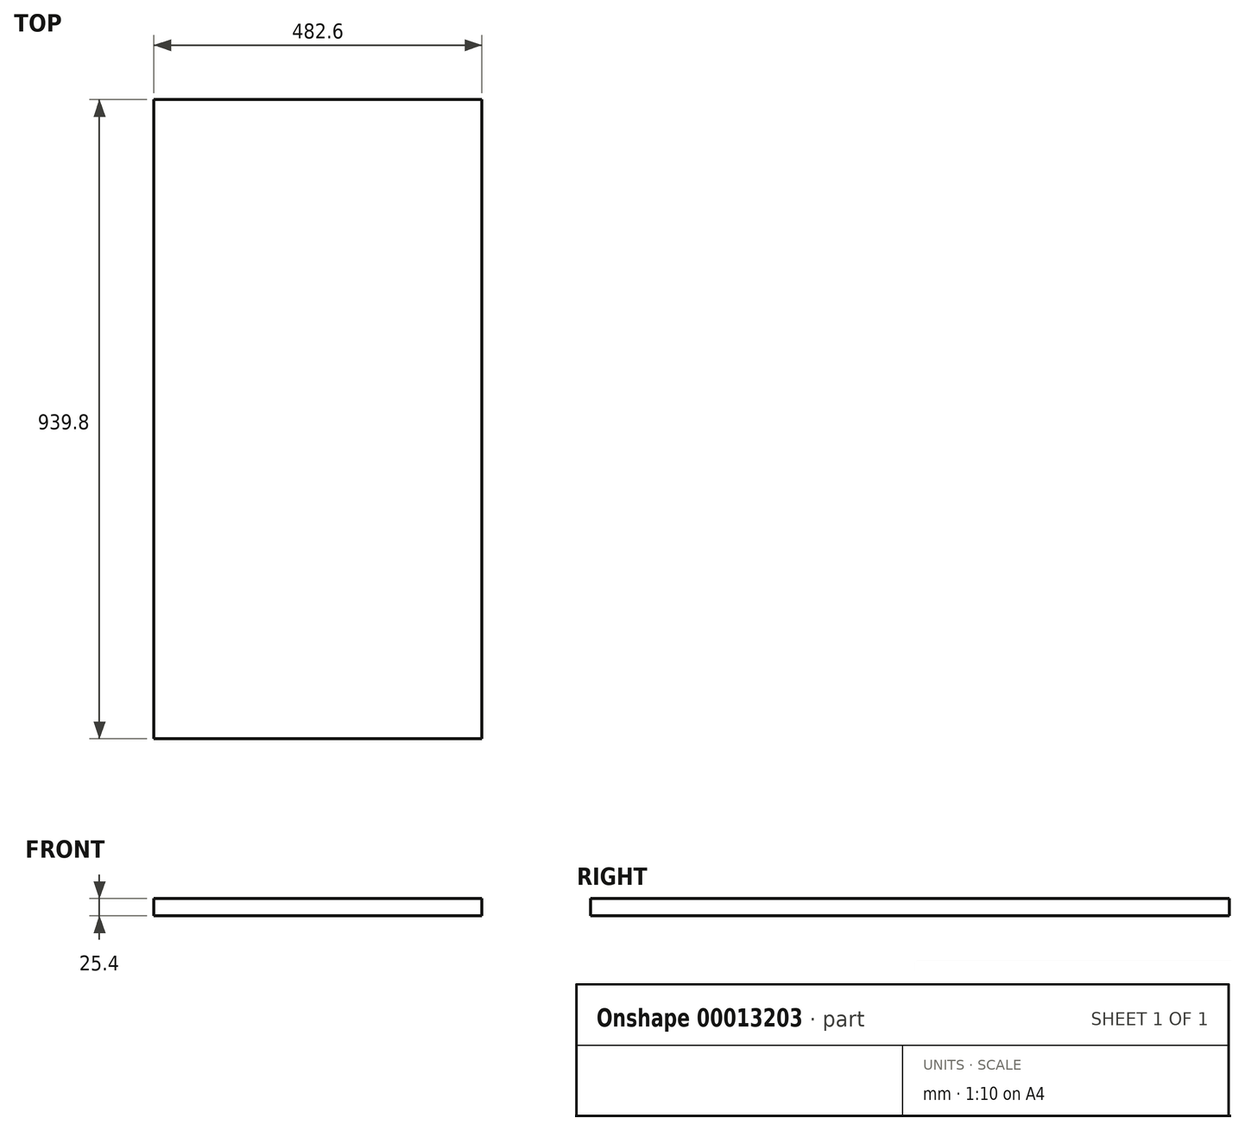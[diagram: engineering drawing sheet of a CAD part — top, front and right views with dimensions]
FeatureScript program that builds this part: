
annotation { "Feature Type Name" : "Feature", "Feature Type Description" : "" }
export const myFeature = defineFeature(function(context is Context, id is Id, definition is map)
    precondition{}
    {
        {
            var Q0;
            Q0=qCreatedBy(makeId("Top.planeOp"),FACE);
            var sketch = newSketch(context, id + "F0", { "sketchPlane" : qUnion([Q0])});
            skLineSegment(sketch, "E0.rect.bottom", {"start": v(-241.3, -469.9) * mm, "end": v(241.3, -469.9) * mm});
            skLineSegment(sketch, "E0.rect.top", {"start": v(-241.3, 469.9) * mm, "end": v(241.3, 469.9) * mm});
            skLineSegment(sketch, "E0.rect.left", {"start": v(-241.3, -469.9) * mm, "end": v(-241.3, 469.9) * mm});
            skLineSegment(sketch, "E0.rect.right", {"start": v(241.3, -469.9) * mm, "end": v(241.3, 469.9) * mm});
            skPoint(sketch, "E0.rect.middle", {"position": v(0, 0) * mm});
            skSolve(sketch);
        }
        {
            var Q0;
            Q0 = qSketchRegion(id + "F0", true);
            extrude(context, id + "F1", {"entities" : qUnion([Q0]), "depth" : 25.4 * mm});
        }
    });
